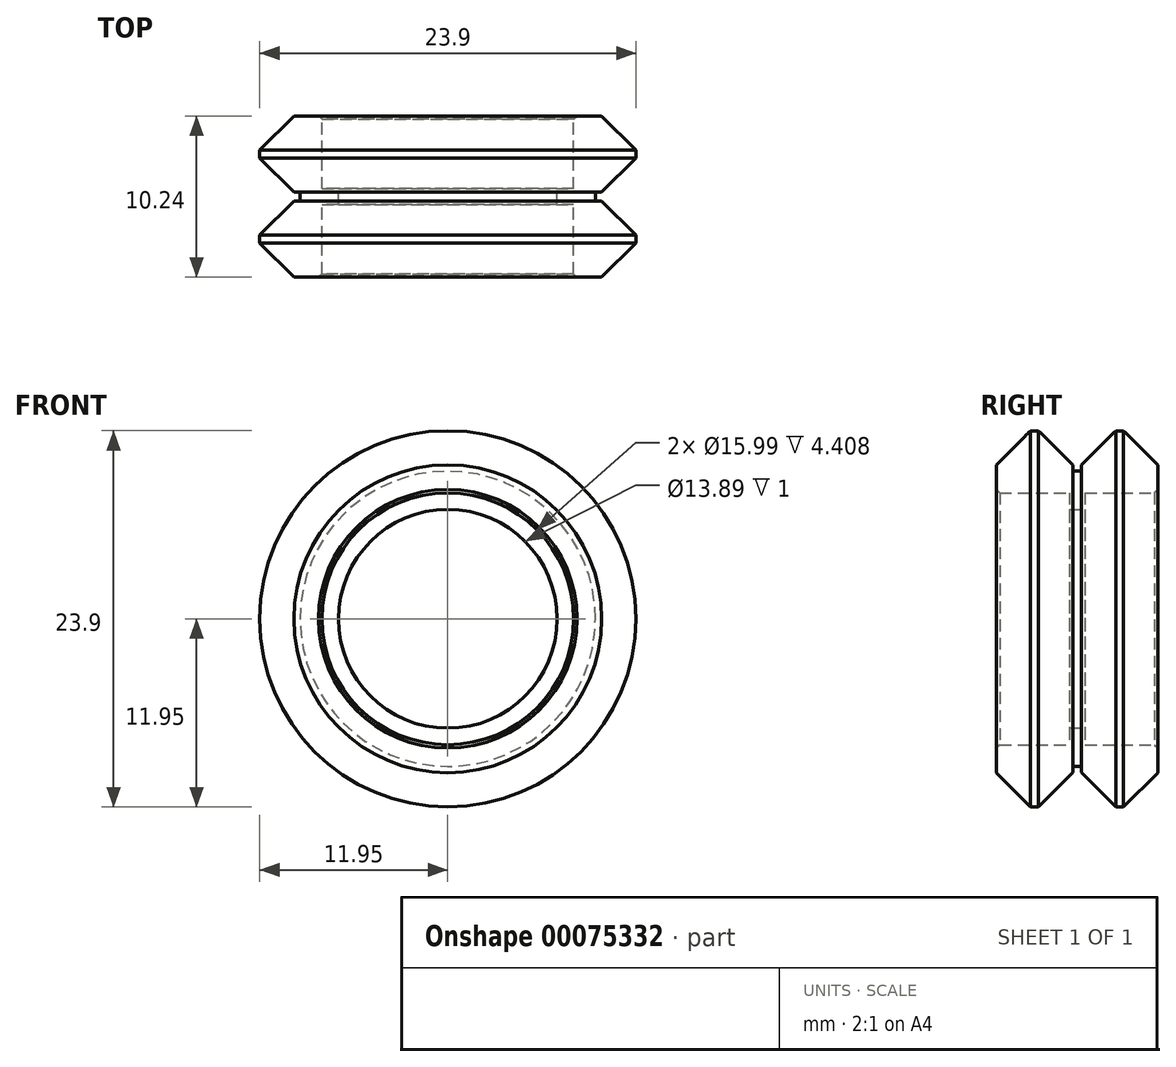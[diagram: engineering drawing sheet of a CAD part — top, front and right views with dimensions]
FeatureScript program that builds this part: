
annotation { "Feature Type Name" : "Feature", "Feature Type Description" : "" }
export const myFeature = defineFeature(function(context is Context, id is Id, definition is map)
    precondition{}
    {
        {
            var Q0;
            Q0=qCreatedBy(makeId("Right.planeOp"),FACE);
            var sketch = newSketch(context, id + "F0", { "sketchPlane" : qUnion([Q0])});
            skLineSegment(sketch, "E0", {"start": v(-0.5, 6.94) * mm, "end": v(-0.5, 8) * mm});
            skLineSegment(sketch, "E1", {"start": v(-0.5, 8) * mm, "end": v(-4.9, 8) * mm});
            skLineSegment(sketch, "E2", {"start": v(-4.9, 8) * mm, "end": v(-5.12, 8.2) * mm});
            skLineSegment(sketch, "E3", {"start": v(-5.12, 8.2) * mm, "end": v(-5.12, 9.78) * mm});
            skLineSegment(sketch, "E4", {"start": v(-5.12, 9.78) * mm, "end": v(-2.95, 11.95) * mm});
            skLineSegment(sketch, "E5", {"start": v(-2.45, 11.95) * mm, "end": v(-0.27, 9.77) * mm});
            skLineSegment(sketch, "E6", {"start": v(9.99, 0) * mm, "end": v(-9.48, 0) * mm, "construction": true});
            skLineSegment(sketch, "E7", {"start": v(-0.5, 6.94) * mm, "end": v(0.5, 6.94) * mm});
            skLineSegment(sketch, "E8", {"start": v(-0.28, 9.77) * mm, "end": v(-0.28, 9.38) * mm});
            skLineSegment(sketch, "E9", {"start": v(-0.27, 9.38) * mm, "end": v(0, 9.38) * mm});
            skLineSegment(sketch, "E10", {"start": v(0, 9.38) * mm, "end": v(0.27, 9.38) * mm});
            skLineSegment(sketch, "E11", {"start": v(0.28, 9.38) * mm, "end": v(0.28, 9.77) * mm});
            skLineSegment(sketch, "E12", {"start": v(0.27, 9.77) * mm, "end": v(2.45, 11.94) * mm});
            skLineSegment(sketch, "E13", {"start": v(2.95, 11.95) * mm, "end": v(5.12, 9.78) * mm});
            skLineSegment(sketch, "E14", {"start": v(5.12, 9.78) * mm, "end": v(5.12, 8.2) * mm});
            skLineSegment(sketch, "E15", {"start": v(5.12, 8.2) * mm, "end": v(4.9, 8) * mm});
            skLineSegment(sketch, "E16", {"start": v(4.9, 8) * mm, "end": v(0.5, 8) * mm});
            skLineSegment(sketch, "E17", {"start": v(0.5, 8) * mm, "end": v(0.5, 6.94) * mm});
            skLineSegment(sketch, "E18", {"start": v(-2.95, 11.95) * mm, "end": v(-2.45, 11.95) * mm});
            skPoint(sketch, "E19.orphan", {"position": v(-2.7, 12.2) * mm});
            skPoint(sketch, "E20.orphan", {"position": v(2.7, 12.2) * mm});
            skLineSegment(sketch, "E21.trimOffspring", {"start": v(2.45, 11.95) * mm, "end": v(2.95, 11.95) * mm});
            skSolve(sketch);
        }
        {
            var Q0;
            Q0=qSketchRegion(id+"F0",true);
            var Q1;
            Q1=sQuery(id+"F0.wireOp",EDGE,"E6");
            revolve(context, id + "F1", {"entities" : qUnion([Q0]), "axis" : qUnion([Q1]), "revolveType" : RevolveType.FULL});
        }
    });
